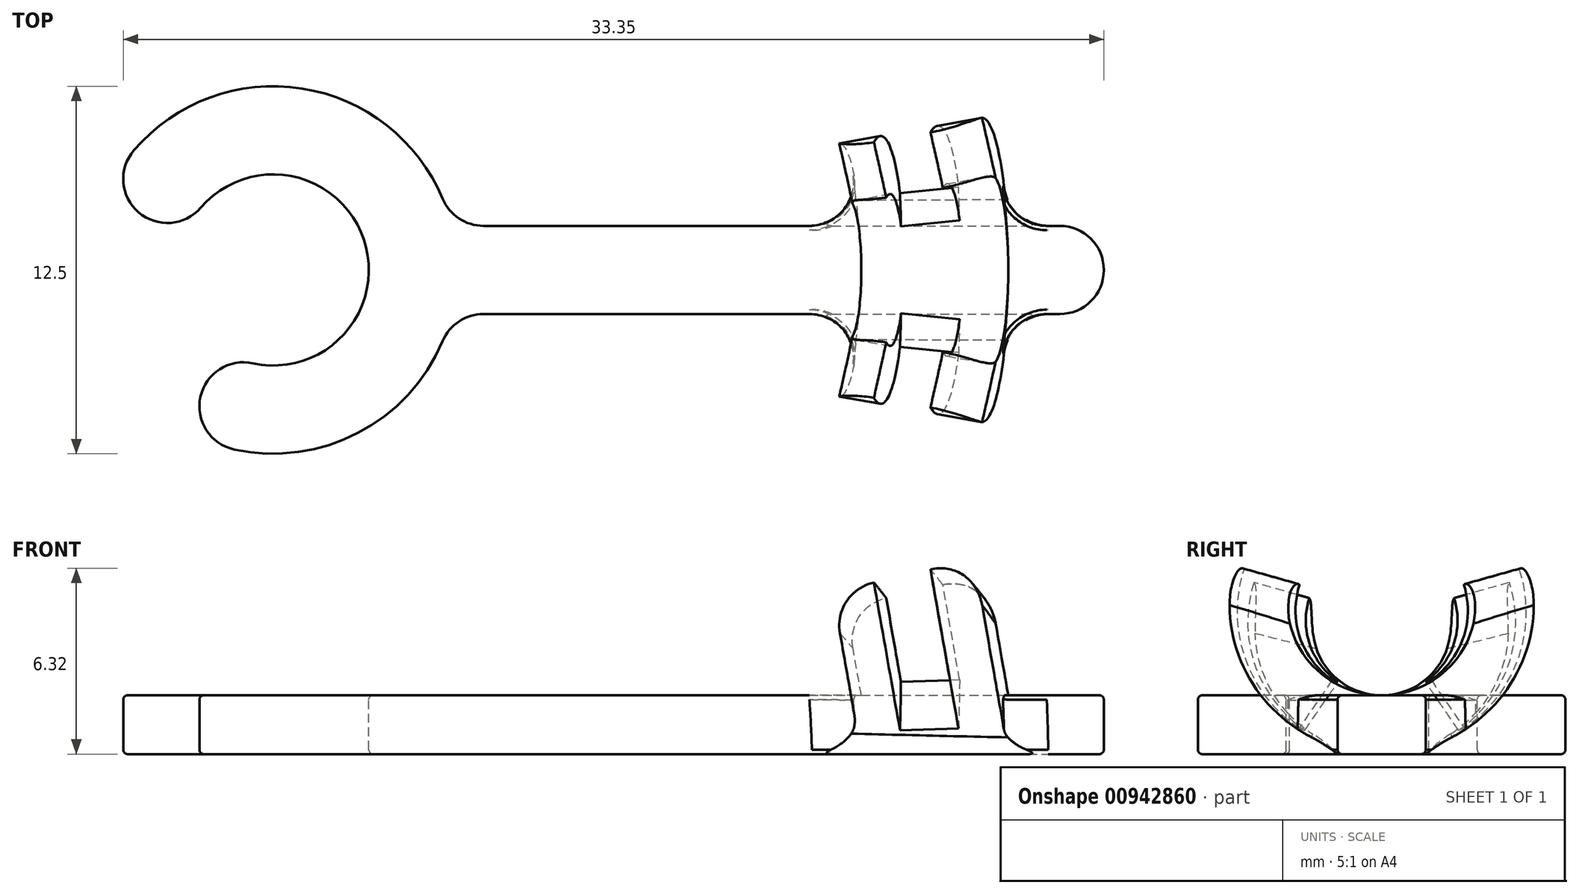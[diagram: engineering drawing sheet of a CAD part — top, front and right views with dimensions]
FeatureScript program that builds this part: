
annotation { "Feature Type Name" : "Feature", "Feature Type Description" : "" }
export const myFeature = defineFeature(function(context is Context, id is Id, definition is map)
    precondition{}
    {
        {
            var Q0;
            Q0=qCreatedBy(makeId("Top.planeOp"),FACE);
            var sketch = newSketch(context, id + "F0", { "sketchPlane" : qUnion([Q0])});
            skLineSegment(sketch, "E0.bottom", {"start": v(0, -1.5) * mm, "end": v(25, -1.5) * mm});
            skLineSegment(sketch, "E0.top", {"start": v(0, 1.5) * mm, "end": v(25, 1.5) * mm});
            skLineSegment(sketch, "E0.left", {"start": v(0, -1.5) * mm, "end": v(0, 1.5) * mm});
            skLineSegment(sketch, "E0.right", {"start": v(25, -1.5) * mm, "end": v(25, 1.5) * mm});
            skSolve(sketch);
        }
        {
            var Q0;
            Q0=qSketchRegion(id+"F0",true);
            extrude(context, id + "F1", {"entities" : qUnion([Q0]), "depth" : 2 * mm});
        }
        {
            var Q0;
            Q0=qCreatedBy(makeId("Front.planeOp"),FACE);
            var sketch = newSketch(context, id + "F2", { "sketchPlane" : qUnion([Q0])});
            skLineSegment(sketch, "E1.bottom", {"start": v(0, 0) * mm, "end": v(3, 0) * mm});
            skLineSegment(sketch, "E1.top", {"start": v(0, 2) * mm, "end": v(3, 2) * mm});
            skLineSegment(sketch, "E1.left", {"start": v(0, 0) * mm, "end": v(0, 2) * mm});
            skLineSegment(sketch, "E1.right", {"start": v(3, 0) * mm, "end": v(3, 2) * mm});
            skLineSegment(sketch, "E2", {"start": v(-3.25, 5.83) * mm, "end": v(-3.25, -3) * mm});
            skSolve(sketch);
        }
        {
            var Q0;
            Q0=makeQuery(id+"F2.imprint","IMPRINT",FACE,{"disambiguationData":[TD([[makeQuery(id+"F2.imprint","IMPRINT",EDGE,{"derivedFrom":sQuery(id+"F2.wireOp",EDGE,"E1.bottom")}),1.0]])]});
            var Q1;
            Q1=sQuery(id+"F2.wireOp",EDGE,"E2");
            revolve(context, id + "F3", {"operationType" : NewBodyOperationType.ADD, "entities" : qUnion([Q0]), "axis" : qUnion([Q1]), "revolveType" : RevolveType.TWO_DIRECTIONS, "angle" : 120.7 * degree, "angleBack" : 202.27 * degree});
        }
        {
            var Q0;
            Q0=qCreatedBy(makeId("Front.planeOp"),FACE);
            var sketch = newSketch(context, id + "F4", { "sketchPlane" : qUnion([Q0])});
            skLineSegment(sketch, "E3.bottom", {"start": v(21.75, 0) * mm, "end": v(16.75, 0) * mm});
            skLineSegment(sketch, "E3.top", {"start": v(21.75, 2) * mm, "end": v(16.75, 2) * mm});
            skLineSegment(sketch, "E3.left", {"start": v(21.75, 0) * mm, "end": v(21.75, 2) * mm});
            skLineSegment(sketch, "E3.right", {"start": v(16.75, 0) * mm, "end": v(16.75, 2) * mm});
            skLineSegment(sketch, "E4", {"start": v(14.65, 4) * mm, "end": v(25.16, 5.85) * mm});
            skSolve(sketch);
        }
        {
            var Q0;
            Q0=makeQuery(id+"F4.imprint","IMPRINT",FACE,{"disambiguationData":[TD([[makeQuery(id+"F4.imprint","IMPRINT",EDGE,{"derivedFrom":sQuery(id+"F4.wireOp",EDGE,"E3.bottom")}),-1.0]])]});
            var Q1;
            Q1=sQuery(id+"F4.wireOp",EDGE,"E4");
            revolve(context, id + "F5", {"operationType" : NewBodyOperationType.ADD, "entities" : qUnion([Q0]), "axis" : qUnion([Q1]), "revolveType" : RevolveType.SYMMETRIC, "angle" : 215 * degree});
        }
        {
            var Q0;
            Q0=makeQuery(id+"F3.boolean.opBoolean","INTERSECT",EDGE,{"derivedFrom":[makeQuery(id+"F1.opExtrude","SWEPT_FACE",FACE,{"disambiguationData":[OSD([sQuery(id+"F0.wireOp",EDGE,"E0.bottom")])]}),makeQuery(id+"F3.opRevolve","SWEPT_FACE",FACE,{"disambiguationData":[OSD([sQuery(id+"F2.wireOp",EDGE,"E1.right")])]})]});
            var Q1;
            Q1=makeQuery(id+"F3.boolean.opBoolean","INTERSECT",EDGE,{"derivedFrom":[makeQuery(id+"F1.opExtrude","SWEPT_FACE",FACE,{"disambiguationData":[OSD([sQuery(id+"F0.wireOp",EDGE,"E0.top")])]}),makeQuery(id+"F3.opRevolve","SWEPT_FACE",FACE,{"disambiguationData":[OSD([sQuery(id+"F2.wireOp",EDGE,"E1.right")])]})]});
            var Q2;
            Q2=makeQuery(id+"F3.opRevolve","CAP_EDGE",EDGE,{"disambiguationData":[OSD([sQuery(id+"F2.wireOp",EDGE,"E1.right")])],"isStart":false});
            var Q3;
            Q3=makeQuery(id+"F3.opRevolve","CAP_EDGE",EDGE,{"disambiguationData":[OSD([sQuery(id+"F2.wireOp",EDGE,"E1.left")])],"isStart":false});
            var Q4;
            Q4=makeQuery(id+"F3.opRevolve","CAP_EDGE",EDGE,{"disambiguationData":[OSD([sQuery(id+"F2.wireOp",EDGE,"E1.left")])],"isStart":true});
            var Q5;
            Q5=makeQuery(id+"F3.opRevolve","CAP_EDGE",EDGE,{"disambiguationData":[OSD([sQuery(id+"F2.wireOp",EDGE,"E1.right")])],"isStart":true});
            var Q6;
            Q6=makeQuery(id+"F1.opExtrude","SWEPT_EDGE",EDGE,{"disambiguationData":[OSD([sQuery(id+"F0.wireOp",EDGE,"E0.top"),sQuery(id+"F0.wireOp",EDGE,"E0.right")])]});
            var Q7;
            Q7=makeQuery(id+"F1.opExtrude","SWEPT_EDGE",EDGE,{"disambiguationData":[OSD([sQuery(id+"F0.wireOp",EDGE,"E0.bottom"),sQuery(id+"F0.wireOp",EDGE,"E0.right")])]});
            var Q8;
            Q8=makeQuery(id+"F5.opRevolve","CAP_EDGE",EDGE,{"disambiguationData":[OSD([sQuery(id+"F4.wireOp",EDGE,"E3.right")])],"isStart":true});
            var Q9;
            Q9=makeQuery(id+"F5.opRevolve","CAP_EDGE",EDGE,{"disambiguationData":[OSD([sQuery(id+"F4.wireOp",EDGE,"E3.left")])],"isStart":true});
            var Q10;
            Q10=makeQuery(id+"F5.opRevolve","CAP_EDGE",EDGE,{"disambiguationData":[OSD([sQuery(id+"F4.wireOp",EDGE,"E3.right")])],"isStart":false});
            var Q11;
            Q11=makeQuery(id+"F5.opRevolve","CAP_EDGE",EDGE,{"disambiguationData":[OSD([sQuery(id+"F4.wireOp",EDGE,"E3.left")])],"isStart":false});
            var Q12;
            Q12=makeQuery(id+"F5.boolean.opBoolean","INTERSECT",EDGE,{"derivedFrom":[makeQuery(id+"F1.opExtrude","SWEPT_FACE",FACE,{"disambiguationData":[OSD([sQuery(id+"F0.wireOp",EDGE,"E0.bottom")])]}),makeQuery(id+"F5.opRevolve","SWEPT_FACE",FACE,{"disambiguationData":[OSD([sQuery(id+"F4.wireOp",EDGE,"E3.left")])]})]});
            var Q13;
            Q13=makeQuery(id+"F5.boolean.opBoolean","INTERSECT",EDGE,{"derivedFrom":[makeQuery(id+"F1.opExtrude","SWEPT_FACE",FACE,{"disambiguationData":[OSD([sQuery(id+"F0.wireOp",EDGE,"E0.top")])]}),makeQuery(id+"F5.opRevolve","SWEPT_FACE",FACE,{"disambiguationData":[OSD([sQuery(id+"F4.wireOp",EDGE,"E3.left")])]})]});
            var Q14;
            Q14=makeQuery(id+"F5.boolean.opBoolean","INTERSECT",EDGE,{"derivedFrom":[makeQuery(id+"F1.opExtrude","SWEPT_FACE",FACE,{"disambiguationData":[OSD([sQuery(id+"F0.wireOp",EDGE,"E0.bottom")])]}),makeQuery(id+"F5.opRevolve","SWEPT_FACE",FACE,{"disambiguationData":[OSD([sQuery(id+"F4.wireOp",EDGE,"E3.right")])]})]});
            var Q15;
            Q15=makeQuery(id+"F5.boolean.opBoolean","INTERSECT",EDGE,{"derivedFrom":[makeQuery(id+"F1.opExtrude","SWEPT_FACE",FACE,{"disambiguationData":[OSD([sQuery(id+"F0.wireOp",EDGE,"E0.top")])]}),makeQuery(id+"F5.opRevolve","SWEPT_FACE",FACE,{"disambiguationData":[OSD([sQuery(id+"F4.wireOp",EDGE,"E3.right")])]})]});
            fillet(context, id + "F6", {"entities" : qUnion([Q0, Q1, Q2, Q3, Q4, Q5, Q6, Q7, Q8, Q9, Q10, Q11, Q12, Q13, Q14, Q15]), "radius" : 1.5 * mm, "tangentPropagation" : true, "allowEdgeOverflow" : false});
        }
        {
            var Q0;
            Q0=makeQuery(id+"F5.boolean.opBoolean","INTERSECT",EDGE,{"derivedFrom":[makeQuery(id+"F1.opExtrude","SWEPT_FACE",FACE,{"disambiguationData":[OSD([sQuery(id+"F0.wireOp",EDGE,"E0.bottom")])]}),makeQuery(id+"F5.opRevolve","SWEPT_FACE",FACE,{"disambiguationData":[OSD([sQuery(id+"F4.wireOp",EDGE,"E3.bottom")])]})]});
            var Q1;
            Q1=makeQuery(id+"F5.boolean.opBoolean","INTERSECT",EDGE,{"derivedFrom":[makeQuery(id+"F1.opExtrude","SWEPT_FACE",FACE,{"disambiguationData":[OSD([sQuery(id+"F0.wireOp",EDGE,"E0.top")])]}),makeQuery(id+"F5.opRevolve","SWEPT_FACE",FACE,{"disambiguationData":[OSD([sQuery(id+"F4.wireOp",EDGE,"E3.bottom")])]})]});
            fillet(context, id + "F7", {"entities" : qUnion([Q0, Q1]), "radius" : 5 * mm, "tangentPropagation" : true, "allowEdgeOverflow" : false});
        }
        {
            var Q0;
            Q0=makeQuery(id+"F1.opExtrude","CAP_EDGE",EDGE,{"disambiguationData":[OSD([sQuery(id+"F0.wireOp",EDGE,"E0.bottom")])],"isStart":true});
            var Q1;
            {var subQ0=sQuery(id+"F0.wireOp",EDGE,"E0.right");var subQ1=sQuery(id+"F0.wireOp",EDGE,"E0.top");Q1=makeQuery(id+"F5.boolean.opBoolean","SPLIT",EDGE,{"disambiguationData":[TD([makeQuery(id+"F1.opExtrude","SWEPT_FACE",FACE,{"disambiguationData":[OSD([subQ0])]})])],"derivedFrom":makeQuery(id+"F1.opExtrude","CAP_EDGE",EDGE,{"disambiguationData":[OSD([subQ1])],"isStart":false})});}
            var Q2;
            {var subQ0=sQuery(id+"F0.wireOp",EDGE,"E0.top");Q2=makeQuery(id+"F5.boolean.opBoolean","SPLIT",EDGE,{"disambiguationData":[TD([makeQuery(id+"F3.opRevolve","SWEPT_FACE",FACE,{"disambiguationData":[OSD([sQuery(id+"F2.wireOp",EDGE,"E1.right")])]})])],"derivedFrom":makeQuery(id+"F1.opExtrude","CAP_EDGE",EDGE,{"disambiguationData":[OSD([subQ0])],"isStart":false})});}
            fillet(context, id + "F8", {"entities" : qUnion([Q0, Q1, Q2]), "radius" : .15 * mm, "tangentPropagation" : true, "allowEdgeOverflow" : false});
        }
        {
            var Q0;
            Q0=makeQuery(id+"F5.opRevolve","CAP_FACE",FACE,{"disambiguationData":[OSD([sQuery(id+"F4.wireOp",EDGE,"E3.bottom"),sQuery(id+"F4.wireOp",EDGE,"E3.top"),sQuery(id+"F4.wireOp",EDGE,"E3.left"),sQuery(id+"F4.wireOp",EDGE,"E3.right")])],"isStart":false});
            var Q1;
            Q1=makeQuery(id+"F5.opRevolve","CAP_FACE",FACE,{"disambiguationData":[OSD([sQuery(id+"F4.wireOp",EDGE,"E3.bottom"),sQuery(id+"F4.wireOp",EDGE,"E3.top"),sQuery(id+"F4.wireOp",EDGE,"E3.left"),sQuery(id+"F4.wireOp",EDGE,"E3.right")])],"isStart":true});
            var Q2;
            Q2=sQuery(id+"F4.wireOp",EDGE,"E4");
            revolve(context, id + "F9", {"operationType" : NewBodyOperationType.REMOVE, "entities" : qUnion([Q0, Q1]), "axis" : qUnion([Q2]), "revolveType" : RevolveType.SYMMETRIC, "oppositeDirection" : true, "angle" : 145 * degree});
        }
    });
